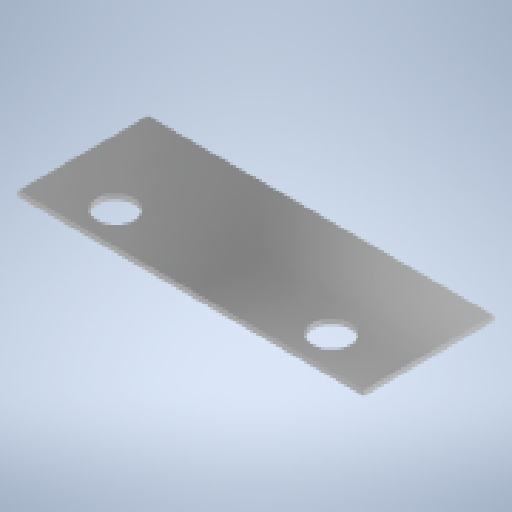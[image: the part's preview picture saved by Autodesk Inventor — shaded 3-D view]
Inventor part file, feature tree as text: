
AUTODESK INVENTOR PART (.ipt)
format: ipt  version: 2023.4 (Build 274418000, 418)  size: 140,800 bytes
history: native  units: in
note: dims shown in document units (in); Inventor stores cm internally (conversion verified against a paired STEP export)
features: other x3, sketch x2
ambient origin geometry x8: Origin, YZ Plane, XZ Plane, XY Plane, X Axis, Y Axis, Z Axis, Center Point
bodies: Solid1 (feature_tree)
feature tree (5):
  other  "GP2-002.ipt"
  other  "Solid1::GP2-002.ipt"
  other  "TaggingFeature1"
  sketch  "Sketch1"  dims[d0=0.3937in]
  sketch  "Sketch2"
